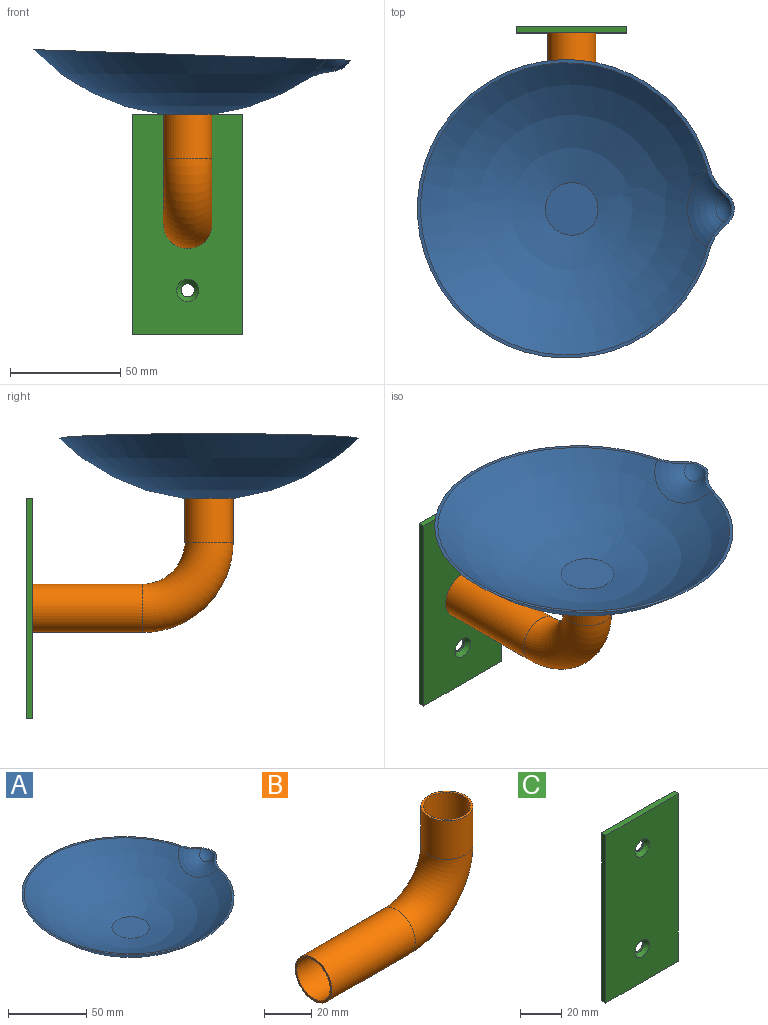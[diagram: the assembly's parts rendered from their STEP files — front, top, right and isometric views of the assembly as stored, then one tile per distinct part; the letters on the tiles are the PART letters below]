
ASSEMBLY  parts=3 mates=2
PART A: 9 faces, bbox 143.8x140x29.9 mm
  f0: plane 143.78x135.48mm, normal (0.03,0,1), area 607.5mm2, adj f1,f2,f3,f5,f6,f7
  f1: sphere r=96.67mm, area 15967.4mm2, adj f0,f3,f4
  f2: sphere r=10mm, area 110.5mm2, adj f0,f3
  f3: torus R=23.03mm, axis (-0.7,0,0.72), area 445.1mm2, adj f0,f1,f2
  f4: plane 24x24mm, normal (0,0,-1), area 452.4mm2, adj f1
  f5: sphere r=95.67mm, area 15241.4mm2, adj f0,f7,f8
  f6: sphere r=9mm, area 82.7mm2, adj f0,f7
  f7: torus R=23.03mm, axis (-0.7,0,0.72), area 420.1mm2, adj f0,f5,f6
  f8: plane 23.88x23.88mm, normal (0,0,1), area 447.7mm2, adj f5
PART B: 8 faces, bbox 94.4x22x64.4 mm
  f0: cylinder r=10mm len=50mm, axis (1,0,0), area 3141.6mm2, adj f1,f3
  f1: torus R=30mm, axis (0,-1,0), area 2960.9mm2, adj f0,f2
  f2: cylinder r=10mm len=20mm, axis (0,0,1), area 1256.6mm2, adj f1,f4
  f3: plane 22x22mm, normal (-1,0,0), area 66mm2, adj f0,f5
  f4: plane 22x22mm, normal (0,0,1), area 66mm2, adj f2,f7
  f5: cylinder r=11mm len=50mm, axis (1,0,0), area 3455.8mm2, adj f3,f6
  f6: torus R=30mm, axis (0,-1,0), area 3257mm2, adj f5,f7
  f7: cylinder r=11mm len=22mm, axis (0,0,1), area 1382.3mm2, adj f4,f6
PART C: 10 faces, bbox 50x3x100 mm
  f0: plane 50x3mm, normal (0,0,-1), area 150mm2, adj f1,f3,f4,f5
  f1: plane 100x3mm, normal (1,0,0), area 300mm2, adj f0,f2,f4,f5
  f2: plane 50x3mm, normal (0,0,1), area 150mm2, adj f1,f3,f4,f5
  f3: plane 100x3mm, normal (-1,0,0), area 300mm2, adj f0,f2,f4,f5
  f4: plane 100x50mm, normal (0,1,0), area 4943.5mm2, adj f0,f1,f2,f3,f6,f8
  f5: plane 100x50mm, normal (0,-1,0), area 4842.9mm2, adj f0,f1,f2,f3,f7,f9
  f6: cylinder r=3mm len=6mm, axis (0,-1,0), area 18.8mm2, adj f4,f7
  f7: cone r=3mm half-angle=45deg, axis (0,-1,0), area 71.1mm2, adj f5,f6
  f8: cylinder r=3mm len=6mm, axis (0,-1,0), area 18.8mm2, adj f4,f9
  f9: cone r=3mm half-angle=45deg, axis (0,-1,0), area 71.1mm2, adj f5,f8
PLACE A t=(-64.13,-37.6,-16.24)mm
PLACE B rot(axis=(0,0,-1),90deg) t=(-64.13,-37.6,-65.49)mm
PLACE C t=(-64.13,42.4,-65.49)mm
MATE fastened B.f0 <-> C.f5  axis (0,-1,0) through (-64.13,42.4,-65.49)mm
MATE fastened B.f2 <-> A.f4  axis (0,0,1) through (-64.13,-37.6,-15.49)mm
